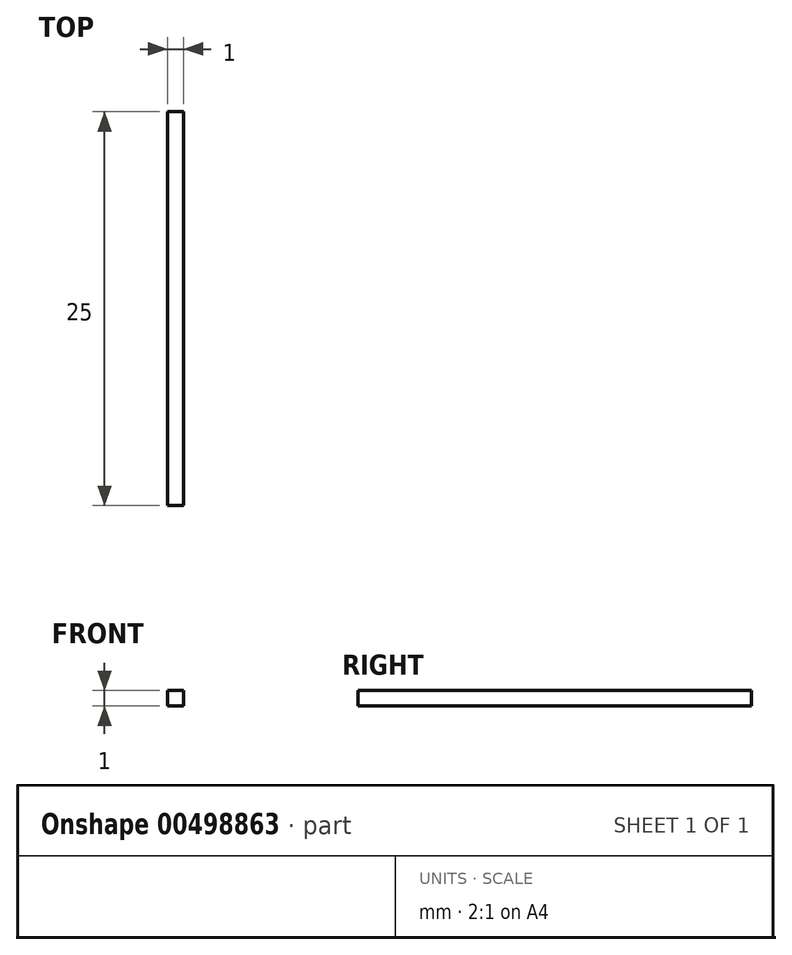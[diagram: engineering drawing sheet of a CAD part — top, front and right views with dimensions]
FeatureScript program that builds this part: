
annotation { "Feature Type Name" : "Feature", "Feature Type Description" : "" }
export const myFeature = defineFeature(function(context is Context, id is Id, definition is map)
    precondition{}
    {
        {
            var Q0;
            Q0=qCreatedBy(makeId("Top.planeOp"),FACE);
            var sketch = newSketch(context, id + "F0", { "sketchPlane" : qUnion([Q0])});
            skLineSegment(sketch, "E0.bottom", {"start": v(-0.5, 12.5) * mm, "end": v(0.5, 12.5) * mm});
            skLineSegment(sketch, "E0.top", {"start": v(-0.5, -12.5) * mm, "end": v(0.5, -12.5) * mm});
            skLineSegment(sketch, "E0.left", {"start": v(-0.5, 12.5) * mm, "end": v(-0.5, -12.5) * mm});
            skLineSegment(sketch, "E0.right", {"start": v(0.5, 12.5) * mm, "end": v(0.5, -12.5) * mm});
            skPoint(sketch, "E0.middle", {"position": v(0, 0) * mm});
            skSolve(sketch);
        }
        {
            var Q0;
            Q0=makeQuery(id+"F0.imprint","IMPRINT",FACE,{"disambiguationData":[TD([[makeQuery(id+"F0.imprint","IMPRINT",EDGE,{"derivedFrom":sQuery(id+"F0.wireOp",EDGE,"E0.bottom")}),-1.0]])]});
            extrude(context, id + "F1", {"entities" : qUnion([Q0]), "depth" : 1 * mm, "offsetDistance" : 25 * mm});
        }
    });
